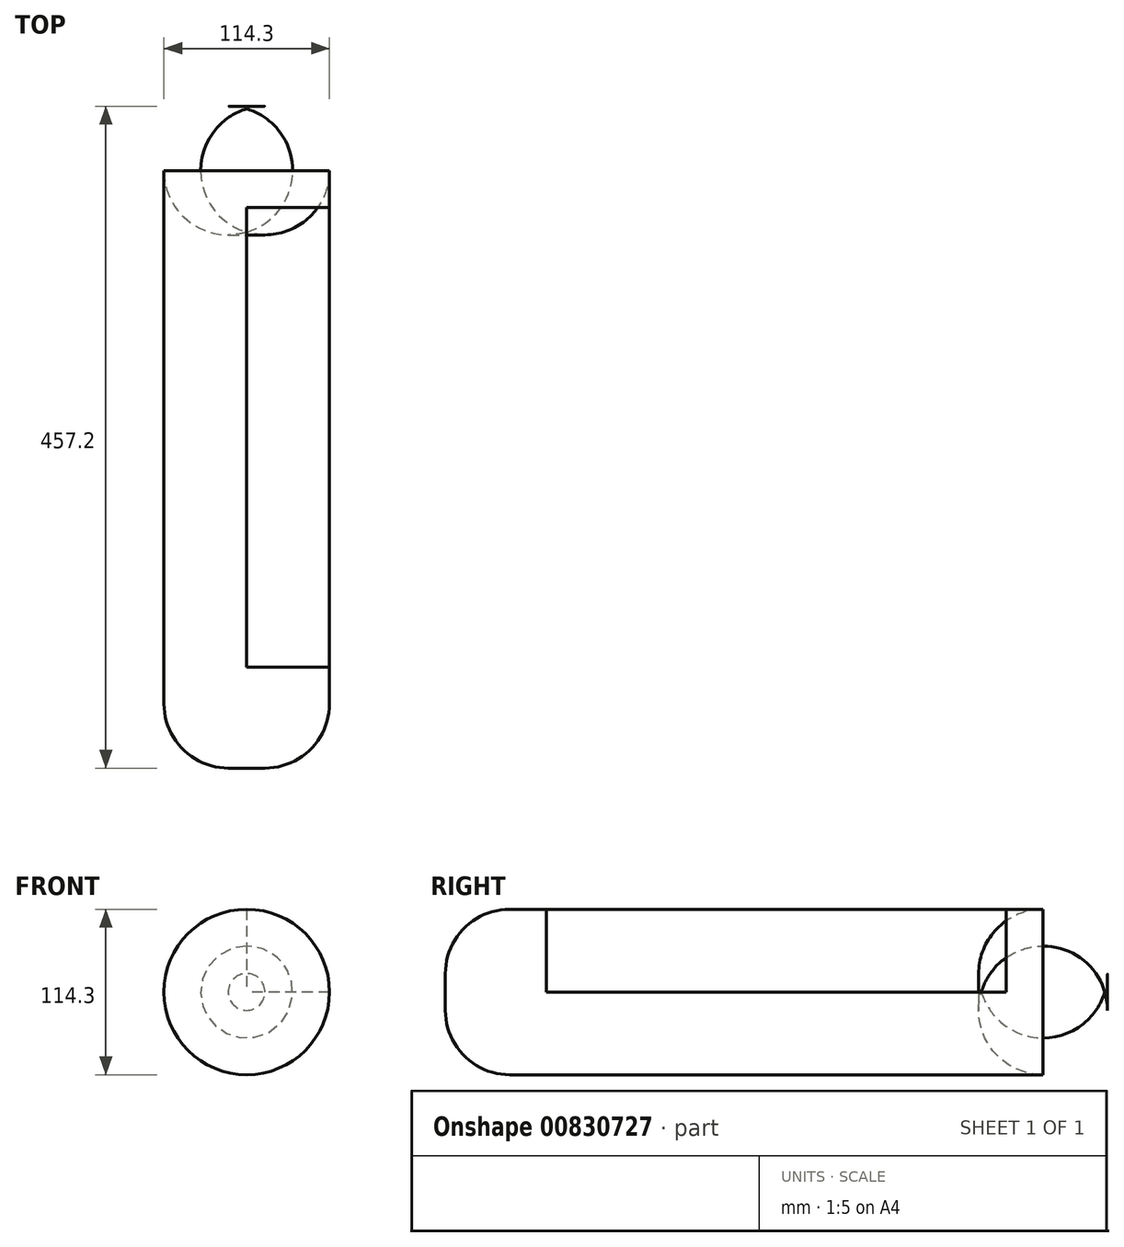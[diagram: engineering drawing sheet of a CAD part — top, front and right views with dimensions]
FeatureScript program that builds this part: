
annotation { "Feature Type Name" : "Feature", "Feature Type Description" : "" }
export const myFeature = defineFeature(function(context is Context, id is Id, definition is map)
    precondition{}
    {
        {
            var Q0;
            Q0=qCreatedBy(makeId("Front.planeOp"),FACE);
            var sketch = newSketch(context, id + "F0", { "sketchPlane" : qUnion([Q0])});
            skCircle(sketch, "E0", {"center": v(0, 0) * mm, "radius": 57.15 * mm});
            skSolve(sketch);
        }
        {
            var Q0;
            Q0 = qSketchRegion(id + "F0", true);
            extrude(context, id + "F1", {"entities" : qUnion([Q0]), "endBound" : BoundingType.SYMMETRIC, "depth" : 457.2 * mm, "offsetDistance" : 25.4 * mm});
        }
        {
            var Q0;
            Q0=makeQuery(id+"F1.opExtrude","CAP_EDGE",EDGE,{"disambiguationData":[OSD([sQuery(id+"F0.wireOp",EDGE,"E0")])],"isStart":false});
            var Q1;
            Q1=makeQuery(id+"F1.opExtrude","CAP_EDGE",EDGE,{"disambiguationData":[OSD([sQuery(id+"F0.wireOp",EDGE,"E0")])],"isStart":true});
            fillet(context, id + "F2", {"entities" : qUnion([Q0, Q1]), "radius" : 44.45 * mm, "tangentPropagation" : true, "allowEdgeOverflow" : false});
        }
        {
            var Q0;
            Q0=qCreatedBy(makeId("Right.planeOp"),FACE);
            var sketch = newSketch(context, id + "F3", { "sketchPlane" : qUnion([Q0])});
            skLineSegment(sketch, "E1.bottom", {"start": v(-158.75, 76.2) * mm, "end": v(158.75, 76.2) * mm});
            skLineSegment(sketch, "E1.top", {"start": v(-158.75, 0) * mm, "end": v(158.75, 0) * mm});
            skLineSegment(sketch, "E1.left", {"start": v(-158.75, 76.2) * mm, "end": v(-158.75, 0) * mm});
            skLineSegment(sketch, "E1.right", {"start": v(158.75, 76.2) * mm, "end": v(158.75, 0) * mm});
            skSolve(sketch);
        }
        {
            var Q0;
            Q0 = qSketchRegion(id + "F3", true);
            extrude(context, id + "F4", {"entities" : qUnion([Q0]), "operationType" : NewBodyOperationType.REMOVE, "endBound" : BoundingType.THROUGH_ALL, "depth" : 25.4 * mm, "offsetDistance" : 25.4 * mm});
        }
    });
